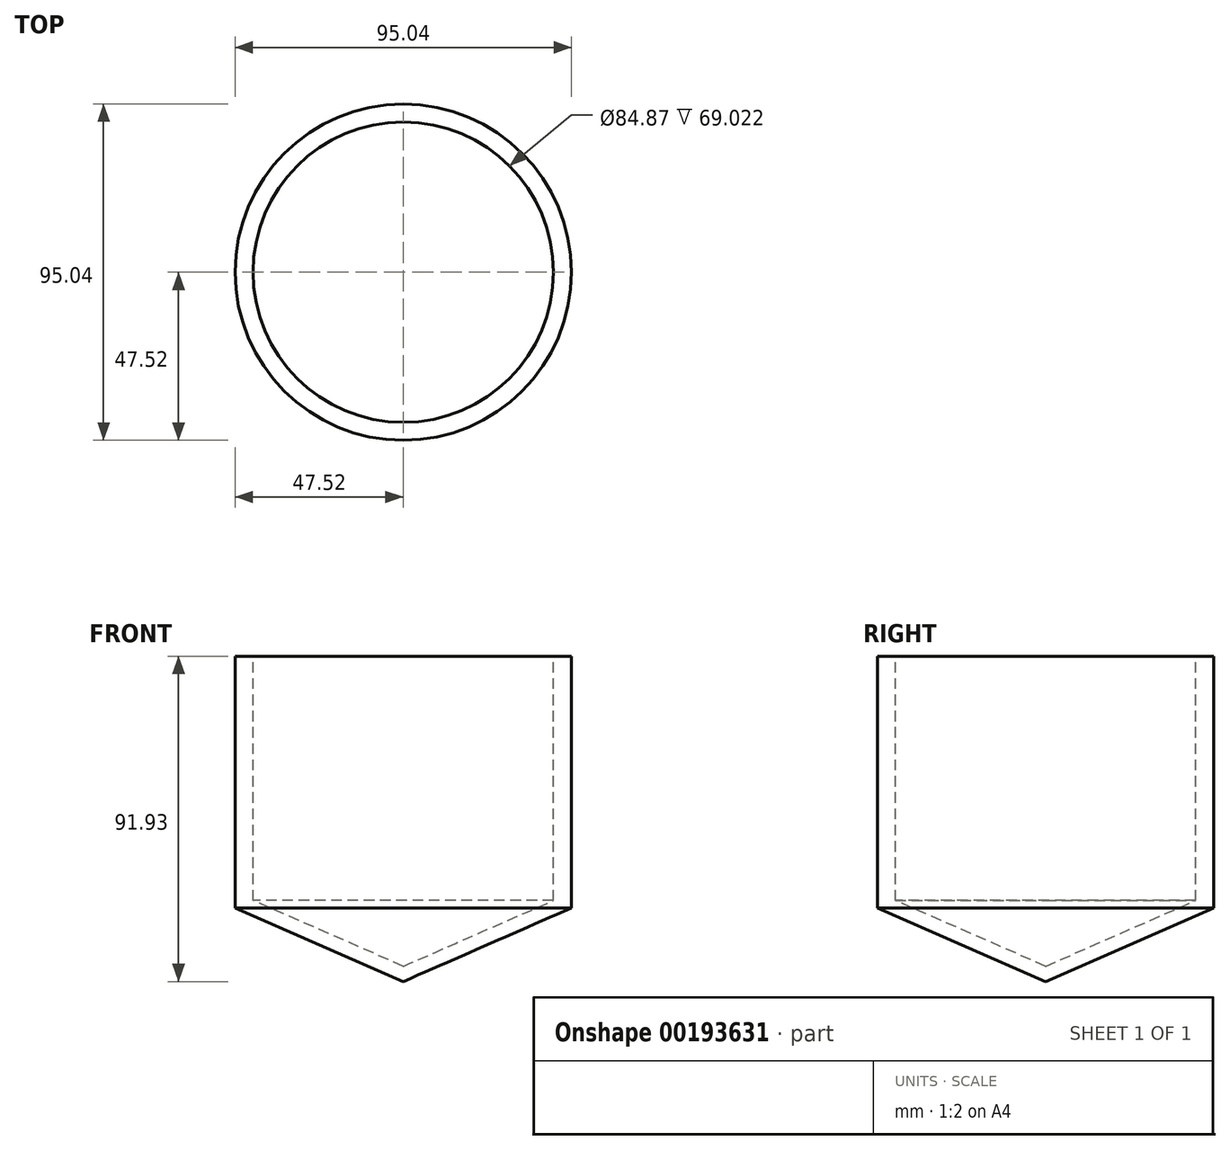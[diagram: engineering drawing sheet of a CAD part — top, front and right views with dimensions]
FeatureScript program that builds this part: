
annotation { "Feature Type Name" : "Feature", "Feature Type Description" : "" }
export const myFeature = defineFeature(function(context is Context, id is Id, definition is map)
    precondition{}
    {
        {
            var Q0;
            Q0=qCreatedBy(makeId("Front.planeOp"),FACE);
            var sketch = newSketch(context, id + "F0", { "sketchPlane" : qUnion([Q0])});
            skLineSegment(sketch, "E0", {"start": v(0, 45.77) * mm, "end": v(0, -46.2) * mm});
            skLineSegment(sketch, "E1", {"start": v(42.44, 45.74) * mm, "end": v(42.44, -23.28) * mm});
            skLineSegment(sketch, "E2", {"start": v(42.44, -23.28) * mm, "end": v(0, -41.87) * mm});
            skLineSegment(sketch, "E3", {"start": v(0, -41.87) * mm, "end": v(0, -46.2) * mm});
            skLineSegment(sketch, "E4", {"start": v(0, -46.2) * mm, "end": v(47.52, -25.38) * mm});
            skLineSegment(sketch, "E5", {"start": v(47.52, -25.38) * mm, "end": v(47.52, 45.74) * mm});
            skLineSegment(sketch, "E6", {"start": v(47.52, 45.74) * mm, "end": v(42.44, 45.74) * mm});
            skSolve(sketch);
        }
        {
            var Q0;
            Q0 = qSketchRegion(id + "F0", true);
            var Q1;
            Q1=sQuery(id+"F0.wireOp",EDGE,"E0");
            revolve(context, id + "F1", {"entities" : qUnion([Q0]), "axis" : qUnion([Q1]), "revolveType" : RevolveType.FULL});
        }
    });
